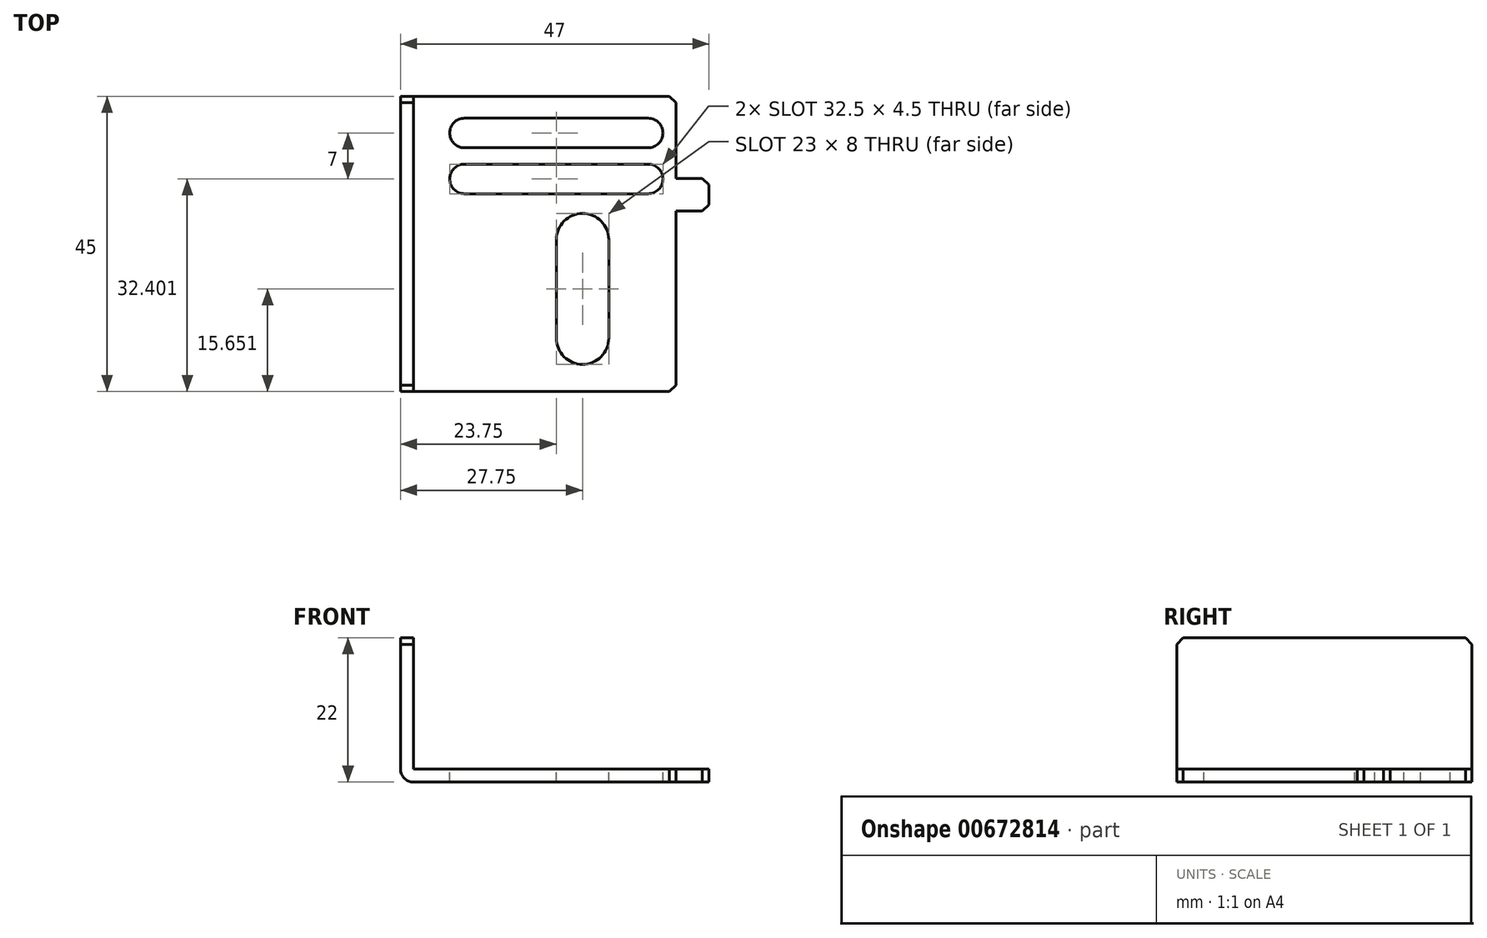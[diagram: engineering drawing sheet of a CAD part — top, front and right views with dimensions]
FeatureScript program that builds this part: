
annotation { "Feature Type Name" : "Feature", "Feature Type Description" : "" }
export const myFeature = defineFeature(function(context is Context, id is Id, definition is map)
    precondition{}
    {
        {
            var Q0;
            Q0=qCreatedBy(makeId("Front.planeOp"),FACE);
            var sketch = newSketch(context, id + "F0", { "sketchPlane" : qUnion([Q0])});
            skLineSegment(sketch, "E0", {"start": v(40, -1) * mm, "end": v(0, -1) * mm});
            skLineSegment(sketch, "E1", {"start": v(-2, 21) * mm, "end": v(-2, 1) * mm});
            skLineSegment(sketch, "E2", {"start": v(40, -1) * mm, "end": v(40, 1) * mm});
            skLineSegment(sketch, "E3", {"start": v(40, 1) * mm, "end": v(0, 1) * mm});
            skLineSegment(sketch, "E4", {"start": v(0, 1) * mm, "end": v(0, 21) * mm});
            skLineSegment(sketch, "E5", {"start": v(13.8, 0) * mm, "end": v(-9.83, 0) * mm, "construction": true});
            skLineSegment(sketch, "E6", {"start": v(0, 21) * mm, "end": v(-2, 21) * mm});
            skLineSegment(sketch, "E7", {"start": v(-1, 46.07) * mm, "end": v(-1, -4.44) * mm, "construction": true});
            skArc(sketch, "E8", {"start": v(-2, 1) * mm, "mid": v(-1.41, -0.41) * mm, "end": v(0, -1) * mm});
            skSolve(sketch);
        }
        {
            var Q0;
            Q0=makeQuery(id+"F0.imprint","IMPRINT",FACE,{"disambiguationData":[TD([[makeQuery(id+"F0.imprint","IMPRINT",EDGE,{"derivedFrom":sQuery(id+"F0.wireOp",EDGE,"E0")}),-1.0]])]});
            extrude(context, id + "F1", {"entities" : qUnion([Q0]), "depth" : 30 * mm, "offsetDistance" : 25 * mm, "hasSecondDirection" : true, "secondDirectionOppositeDirection" : true, "secondDirectionDepth" : 15 * mm});
        }
        {
            var Q0;
            Q0=makeQuery(id+"F1.opExtrude","SWEPT_FACE",FACE,{"disambiguationData":[OSD([sQuery(id+"F0.wireOp",EDGE,"E3")])]});
            var sketch = newSketch(context, id + "F2", { "sketchPlane" : qUnion([Q0])});
            skLineSegment(sketch, "E9", {"start": v(7.75, 11.65) * mm, "end": v(35.75, 11.65) * mm});
            skLineSegment(sketch, "E10", {"start": v(7.75, 7.15) * mm, "end": v(35.75, 7.15) * mm});
            skLineSegment(sketch, "E11", {"start": v(20.02, 9.4) * mm, "end": v(52.47, 9.4) * mm, "construction": true});
            skLineSegment(sketch, "E12", {"start": v(7.75, 13.82) * mm, "end": v(7.75, -3.56) * mm, "construction": true});
            skLineSegment(sketch, "E13", {"start": v(35.75, 13.31) * mm, "end": v(35.75, -5.54) * mm, "construction": true});
            skArc(sketch, "E14", {"start": v(35.75, 7.15) * mm, "mid": v(38, 9.4) * mm, "end": v(35.75, 11.65) * mm});
            skArc(sketch, "E15", {"start": v(7.75, 11.65) * mm, "mid": v(5.5, 9.4) * mm, "end": v(7.75, 7.15) * mm});
            skLineSegment(sketch, "E16", {"start": v(19.74, -21.85) * mm, "end": v(31.76, -21.85) * mm, "construction": true});
            skArc(sketch, "E17", {"start": v(21.75, -21.85) * mm, "mid": v(25.75, -25.85) * mm, "end": v(29.75, -21.85) * mm});
            skLineSegment(sketch, "E18", {"start": v(7.75, 4.65) * mm, "end": v(35.75, 4.65) * mm});
            skLineSegment(sketch, "E19", {"start": v(7.75, 0.15) * mm, "end": v(35.75, 0.15) * mm});
            skLineSegment(sketch, "E20", {"start": v(25.41, 2.4) * mm, "end": v(57.86, 2.4) * mm, "construction": true});
            skLineSegment(sketch, "E21", {"start": v(35.75, 26.34) * mm, "end": v(35.75, 18.04) * mm, "construction": true});
            skArc(sketch, "E22", {"start": v(35.75, 0.15) * mm, "mid": v(38, 2.4) * mm, "end": v(35.75, 4.65) * mm});
            skArc(sketch, "E23", {"start": v(7.75, 4.65) * mm, "mid": v(5.5, 2.4) * mm, "end": v(7.75, 0.15) * mm});
            skLineSegment(sketch, "E24", {"start": v(21.75, -21.85) * mm, "end": v(21.75, -6.85) * mm});
            skLineSegment(sketch, "E25", {"start": v(29.75, -21.85) * mm, "end": v(29.75, -6.85) * mm});
            skArc(sketch, "E26", {"start": v(29.75, -6.85) * mm, "mid": v(25.75, -2.85) * mm, "end": v(21.75, -6.85) * mm});
            skSolve(sketch);
        }
        {
            var Q0;
            Q0 = qSketchRegion(id + "F2", true);
            extrude(context, id + "F3", {"entities" : qUnion([Q0]), "operationType" : NewBodyOperationType.REMOVE, "oppositeDirection" : true, "depth" : 25 * mm, "offsetDistance" : 25 * mm});
        }
        {
            var Q0;
            Q0=makeQuery(id+"F1.opExtrude","SWEPT_FACE",FACE,{"disambiguationData":[OSD([sQuery(id+"F0.wireOp",EDGE,"E3")])]});
            var sketch = newSketch(context, id + "F4", { "sketchPlane" : qUnion([Q0])});
            skLineSegment(sketch, "E27.bottom", {"start": v(40, -2.5) * mm, "end": v(45, -2.5) * mm});
            skLineSegment(sketch, "E27.top", {"start": v(40, 2.5) * mm, "end": v(45, 2.5) * mm});
            skLineSegment(sketch, "E27.left", {"start": v(40, -2.5) * mm, "end": v(40, 2.5) * mm});
            skLineSegment(sketch, "E27.right", {"start": v(45, -2.5) * mm, "end": v(45, 2.5) * mm});
            skSolve(sketch);
        }
        {
            var Q0;
            Q0 = qSketchRegion(id + "F4", true);
            var Q1;
            Q1=makeQuery(id+"F1.opExtrude","SWEPT_FACE",FACE,{"disambiguationData":[OSD([sQuery(id+"F0.wireOp",EDGE,"E0")])]});
            extrude(context, id + "F5", {"entities" : qUnion([Q0]), "operationType" : NewBodyOperationType.ADD, "endBound" : BoundingType.UP_TO_SURFACE, "oppositeDirection" : true, "depth" : 25 * mm, "endBoundEntityFace" : qUnion([Q1]), "offsetDistance" : 25 * mm});
        }
        {
            var Q0;
            Q0=makeQuery(id+"F1.opExtrude","CAP_EDGE",EDGE,{"disambiguationData":[OSD([sQuery(id+"F0.wireOp",EDGE,"E6")])],"isStart":true});
            var Q1;
            Q1=makeQuery(id+"F1.opExtrude","CAP_EDGE",EDGE,{"disambiguationData":[OSD([sQuery(id+"F0.wireOp",EDGE,"E6")])],"isStart":false});
            var Q2;
            Q2=makeQuery(id+"F1.opExtrude","CAP_EDGE",EDGE,{"disambiguationData":[OSD([sQuery(id+"F0.wireOp",EDGE,"E2")])],"isStart":false});
            var Q3;
            Q3=makeQuery(id+"F1.opExtrude","CAP_EDGE",EDGE,{"disambiguationData":[OSD([sQuery(id+"F0.wireOp",EDGE,"E2")])],"isStart":true});
            var Q4;
            Q4=makeQuery(id+"F5.opExtrude","SWEPT_EDGE",EDGE,{"disambiguationData":[OSD([sQuery(id+"F4.wireOp",EDGE,"E27.top"),sQuery(id+"F4.wireOp",EDGE,"E27.right")])]});
            var Q5;
            Q5=makeQuery(id+"F5.opExtrude","SWEPT_EDGE",EDGE,{"disambiguationData":[OSD([sQuery(id+"F4.wireOp",EDGE,"E27.bottom"),sQuery(id+"F4.wireOp",EDGE,"E27.right")])]});
            chamfer(context, id + "F6", {"entities" : qUnion([Q0, Q1, Q2, Q3, Q4, Q5]), "chamferType" : ChamferType.OFFSET_ANGLE, "width" : 1 * mm, "oppositeDirection" : false, "angle" : 45 * degree, "tangentPropagation" : true});
        }
    });
